# Revit family: Hub_Adapter-Zurn-Z1030
name_source: partatom
category: Plumbing Fixtures
units: mm (PartAtom-declared; Revit-internal decimal feet)

## family parameters
Always vertical = Yes
Cut with Voids When Loaded = No
Maintain Annotation Orientation = No
OmniClass Number = 23.60.30.11.14
OmniClass Title = Pipework Fittings
Part Type = Normal
Room Calculation Point = No
Round Connector Dimension = Use Radius
Shared = No
Work Plane-Based = No

## types (4) — shared parameters
Assembly Code = D2090800
CW Connection = No
Default Elevation = 20 "
Description = HUB ADAPTER
HW Connection = No
Main Material = Iron - Zurn - Cast - Painted - Blue
Manufacturer = Zurn Water, LLC
Manufacurer Brand = Zurn
Model = Z1030
Modified Date = 02/20/2026
Product Documentation Link = https://files.zurn.com
Product Installation Sheet URL = https://files.zurn.com
Product Page URL = https://www.zurn.com
Product data url = https://www.bimobject.com
URL = www.zurn.com
Vent Connection = No
WFU = 1
Waste Connection = Yes
zero-valued in all types: CWFU, HWFU

## per-type parameters (varying)
| type | Approx Weight | Body Height_B | Connector Radius | Hub | Pipe Size_A Inside Diameter | Pipe Size_A Nominal Diameter | Pipe Size_A Outer Diameter |
| Z1030 2 Inch IP x HB | 3.00 lb | 4.25 " | 1 " | 2.683 " | 2.067 " | 2 " | 2.375 " |
| Z1030 3 Inch  IP x HB | 5.00 lb | 4.375 " | 1.5 " | 3.808 " | 3.068 " | 3 " | 3.5 " |
| Z1030 4 Inch IP x HB | 6.00 lb | 4.75 " | 2 " | 4.808 " | 4.026 " | 4 " | 4.5 " |
| Z1030 6 Inch IP x HB | 9.00 lb | 5 " | 3 " | 6.933 " | 6.065 " | 6 " | 6.625 " |

## geometry (parser evidence)
native form markers: Blend x6, Sweep x3
no freeform markers — native parametric forms only
